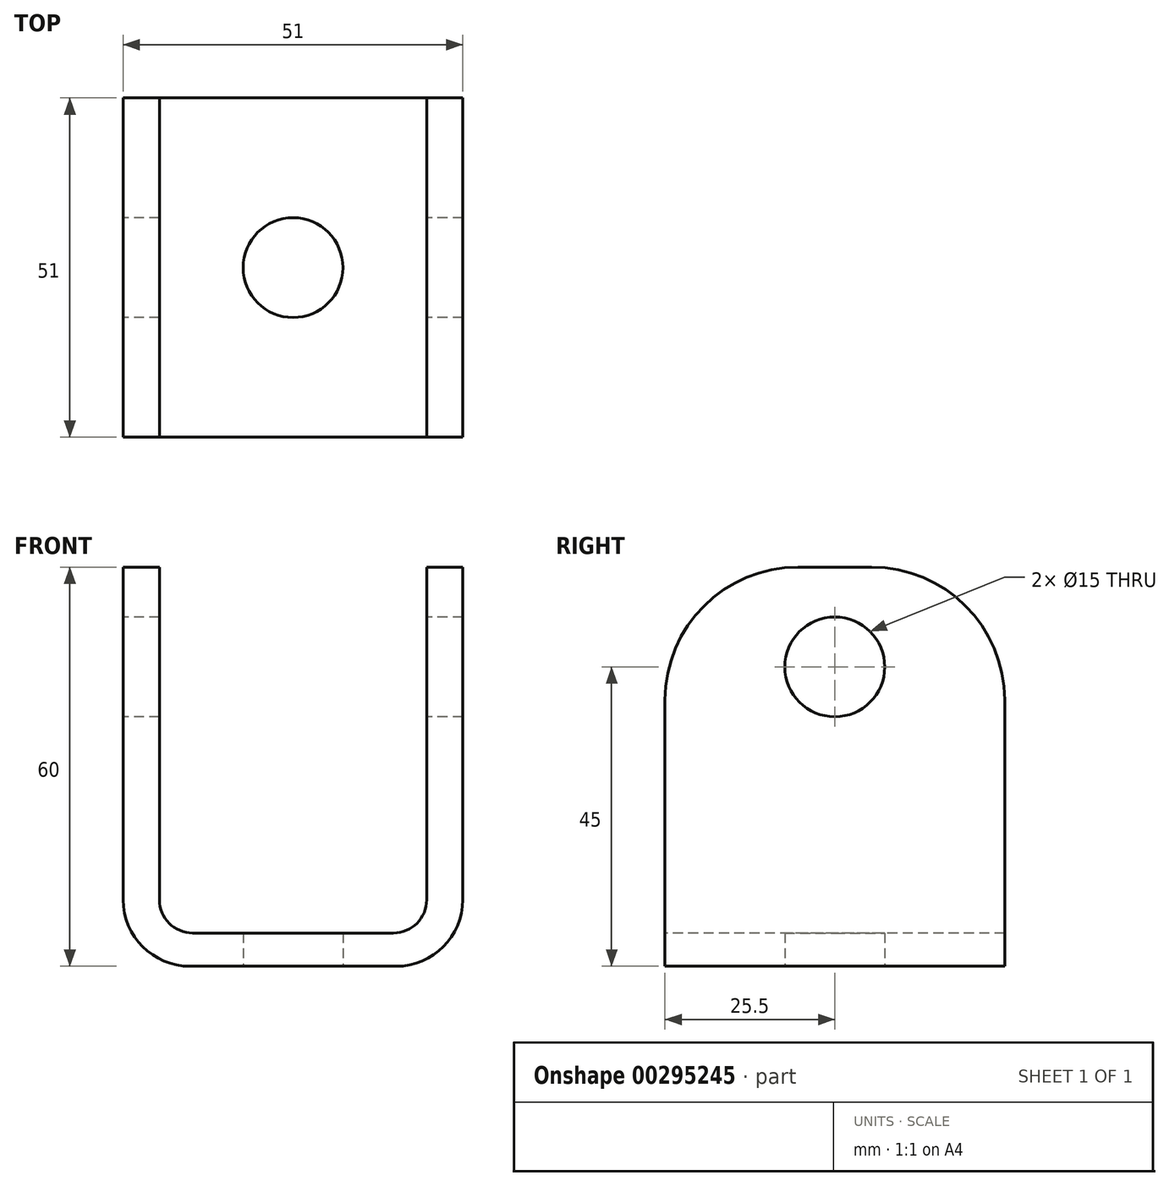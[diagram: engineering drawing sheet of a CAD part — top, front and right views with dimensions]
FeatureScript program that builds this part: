
annotation { "Feature Type Name" : "Feature", "Feature Type Description" : "" }
export const myFeature = defineFeature(function(context is Context, id is Id, definition is map)
    precondition{}
    {
        {
            var Q0;
            Q0=qCreatedBy(makeId("Top.planeOp"),FACE);
            var sketch = newSketch(context, id + "F0", { "sketchPlane" : qUnion([Q0])});
            skLineSegment(sketch, "E0.bottom", {"start": v(-25.5, -25.5) * mm, "end": v(25.5, -25.5) * mm});
            skLineSegment(sketch, "E0.top", {"start": v(-25.5, 25.5) * mm, "end": v(25.5, 25.5) * mm});
            skLineSegment(sketch, "E0.left", {"start": v(-25.5, -25.5) * mm, "end": v(-25.5, 25.5) * mm});
            skLineSegment(sketch, "E0.right", {"start": v(25.5, -25.5) * mm, "end": v(25.5, 25.5) * mm});
            skPoint(sketch, "E0.middle", {"position": v(0, 0) * mm});
            skSolve(sketch);
        }
        {
            var Q0;
            Q0=makeQuery(id+"F0.imprint","IMPRINT",FACE,{"disambiguationData":[TD([[makeQuery(id+"F0.imprint","IMPRINT",EDGE,{"derivedFrom":sQuery(id+"F0.wireOp",EDGE,"E0.bottom")}),1.0]])]});
            extrude(context, id + "F1", {"entities" : qUnion([Q0]), "depth" : 60 * mm});
        }
        {
            var Q0;
            Q0=makeQuery(id+"F1.opExtrude","SWEPT_FACE",FACE,{"disambiguationData":[OSD([sQuery(id+"F0.wireOp",EDGE,"E0.bottom")])]});
            var sketch = newSketch(context, id + "F2", { "sketchPlane" : qUnion([Q0])});
            skLineSegment(sketch, "E1.bottom", {"start": v(-20.07, 60) * mm, "end": v(20.07, 60) * mm});
            skLineSegment(sketch, "E1.top", {"start": v(-20.07, 5) * mm, "end": v(20.07, 5) * mm});
            skLineSegment(sketch, "E1.left", {"start": v(-20.07, 60) * mm, "end": v(-20.07, 5) * mm});
            skLineSegment(sketch, "E1.right", {"start": v(20.07, 60) * mm, "end": v(20.07, 5) * mm});
            skPoint(sketch, "E1.middle", {"position": v(0, 32.5) * mm});
            skPoint(sketch, "E1.middle.positionSnap0", {"position": v(0, 60) * mm});
            skPoint(sketch, "E1.centerSnap0", {"position": v(0, 60) * mm});
            skSolve(sketch);
        }
        {
            var Q0;
            Q0=makeQuery(id+"F2.imprint","IMPRINT",FACE,{"disambiguationData":[TD([[makeQuery(id+"F2.imprint","IMPRINT",EDGE,{"derivedFrom":sQuery(id+"F2.wireOp",EDGE,"E1.bottom")}),-1.0]])]});
            extrude(context, id + "F3", {"entities" : qUnion([Q0]), "operationType" : NewBodyOperationType.REMOVE, "oppositeDirection" : true, "depth" : 51 * mm});
        }
        {
            var Q0;
            Q0=qCreatedBy(makeId("Top.planeOp"),FACE);
            var sketch = newSketch(context, id + "F4", { "sketchPlane" : qUnion([Q0])});
            skCircle(sketch, "E2", {"center": v(0, 0) * mm, "radius": 7.5 * mm});
            skSolve(sketch);
        }
        {
            var Q0;
            Q0=makeQuery(id+"F4.imprint","IMPRINT",FACE,{"disambiguationData":[TD([[makeQuery(id+"F4.imprint","IMPRINT",EDGE,{"derivedFrom":sQuery(id+"F4.wireOp",EDGE,"E2")}),1.0]])]});
            var Q1;
            Q1=sQuery(id+"F4.wireOp",EDGE,"E2");
            extrude(context, id + "F5", {"entities" : qUnion([Q0]), "operationType" : NewBodyOperationType.REMOVE, "surfaceEntities" : qUnion([Q1]), "endBound" : BoundingType.THROUGH_ALL, "depth" : 25 * mm});
        }
        {
            var Q0;
            Q0=qCreatedBy(makeId("Right.planeOp"),FACE);
            var sketch = newSketch(context, id + "F6", { "sketchPlane" : qUnion([Q0])});
            skCircle(sketch, "E3", {"center": v(0, 45) * mm, "radius": 7.5 * mm});
            skSolve(sketch);
        }
        {
            var Q0;
            Q0=makeQuery(id+"F6.imprint","IMPRINT",FACE,{"disambiguationData":[TD([[makeQuery(id+"F6.imprint","IMPRINT",EDGE,{"derivedFrom":sQuery(id+"F6.wireOp",EDGE,"E3")}),1.0]])]});
            extrude(context, id + "F7", {"entities" : qUnion([Q0]), "operationType" : NewBodyOperationType.REMOVE, "endBound" : BoundingType.THROUGH_ALL, "depth" : 25 * mm, "hasSecondDirection" : true, "secondDirectionOppositeDirection" : true, "secondDirectionDepth" : 88.26 * mm});
        }
        {
            var Q0;
            Q0=makeQuery(id+"F1.opExtrude","CAP_EDGE",EDGE,{"disambiguationData":[OSD([sQuery(id+"F0.wireOp",EDGE,"E0.left")])],"isStart":true});
            var Q1;
            Q1=makeQuery(id+"F1.opExtrude","CAP_EDGE",EDGE,{"disambiguationData":[OSD([sQuery(id+"F0.wireOp",EDGE,"E0.right")])],"isStart":true});
            fillet(context, id + "F8", {"entities" : qUnion([Q0, Q1]), "radius" : 10 * mm, "tangentPropagation" : true, "allowEdgeOverflow" : false});
        }
        {
            var Q0;
            Q0=makeQuery(id+"F3.boolean.opBoolean","COPY",EDGE,{"derivedFrom":makeQuery(id+"F3.opExtrude","SWEPT_EDGE",EDGE,{"disambiguationData":[OSD([sQuery(id+"F2.wireOp",EDGE,"E1.top"),sQuery(id+"F2.wireOp",EDGE,"E1.left")])]})});
            var Q1;
            Q1=makeQuery(id+"F3.boolean.opBoolean","COPY",EDGE,{"derivedFrom":makeQuery(id+"F3.opExtrude","SWEPT_EDGE",EDGE,{"disambiguationData":[OSD([sQuery(id+"F2.wireOp",EDGE,"E1.top"),sQuery(id+"F2.wireOp",EDGE,"E1.right")])]})});
            fillet(context, id + "F9", {"entities" : qUnion([Q0, Q1]), "radius" : 5 * mm, "tangentPropagation" : true, "allowEdgeOverflow" : false});
        }
        {
            var Q0;
            {var subQ0=sQuery(id+"F0.wireOp",EDGE,"E0.left");var subQ1=sQuery(id+"F0.wireOp",EDGE,"E0.top");Q0=makeQuery(id+"F3.boolean.opBoolean","SPLIT",EDGE,{"disambiguationData":[TD([makeQuery(id+"F1.opExtrude","SWEPT_FACE",FACE,{"disambiguationData":[OSD([subQ0])]})])],"derivedFrom":makeQuery(id+"F1.opExtrude","CAP_EDGE",EDGE,{"disambiguationData":[OSD([subQ1])],"isStart":false})});}
            var Q1;
            {var subQ0=sQuery(id+"F0.wireOp",EDGE,"E0.bottom");var subQ1=sQuery(id+"F0.wireOp",EDGE,"E0.left");Q1=makeQuery(id+"F3.boolean.opBoolean","SPLIT",EDGE,{"disambiguationData":[TD([makeQuery(id+"F1.opExtrude","SWEPT_FACE",FACE,{"disambiguationData":[OSD([subQ1])]})])],"derivedFrom":makeQuery(id+"F1.opExtrude","CAP_EDGE",EDGE,{"disambiguationData":[OSD([subQ0])],"isStart":false})});}
            var Q2;
            {var subQ0=sQuery(id+"F0.wireOp",EDGE,"E0.right");var subQ1=sQuery(id+"F0.wireOp",EDGE,"E0.top");Q2=makeQuery(id+"F3.boolean.opBoolean","SPLIT",EDGE,{"disambiguationData":[TD([makeQuery(id+"F1.opExtrude","SWEPT_FACE",FACE,{"disambiguationData":[OSD([subQ0])]})])],"derivedFrom":makeQuery(id+"F1.opExtrude","CAP_EDGE",EDGE,{"disambiguationData":[OSD([subQ1])],"isStart":false})});}
            var Q3;
            {var subQ0=sQuery(id+"F0.wireOp",EDGE,"E0.bottom");var subQ1=sQuery(id+"F0.wireOp",EDGE,"E0.right");Q3=makeQuery(id+"F3.boolean.opBoolean","SPLIT",EDGE,{"disambiguationData":[TD([makeQuery(id+"F1.opExtrude","SWEPT_FACE",FACE,{"disambiguationData":[OSD([subQ1])]})])],"derivedFrom":makeQuery(id+"F1.opExtrude","CAP_EDGE",EDGE,{"disambiguationData":[OSD([subQ0])],"isStart":false})});}
            fillet(context, id + "F10", {"entities" : qUnion([Q0, Q1, Q2, Q3]), "radius" : 20 * mm, "tangentPropagation" : true, "allowEdgeOverflow" : false});
        }
    });
